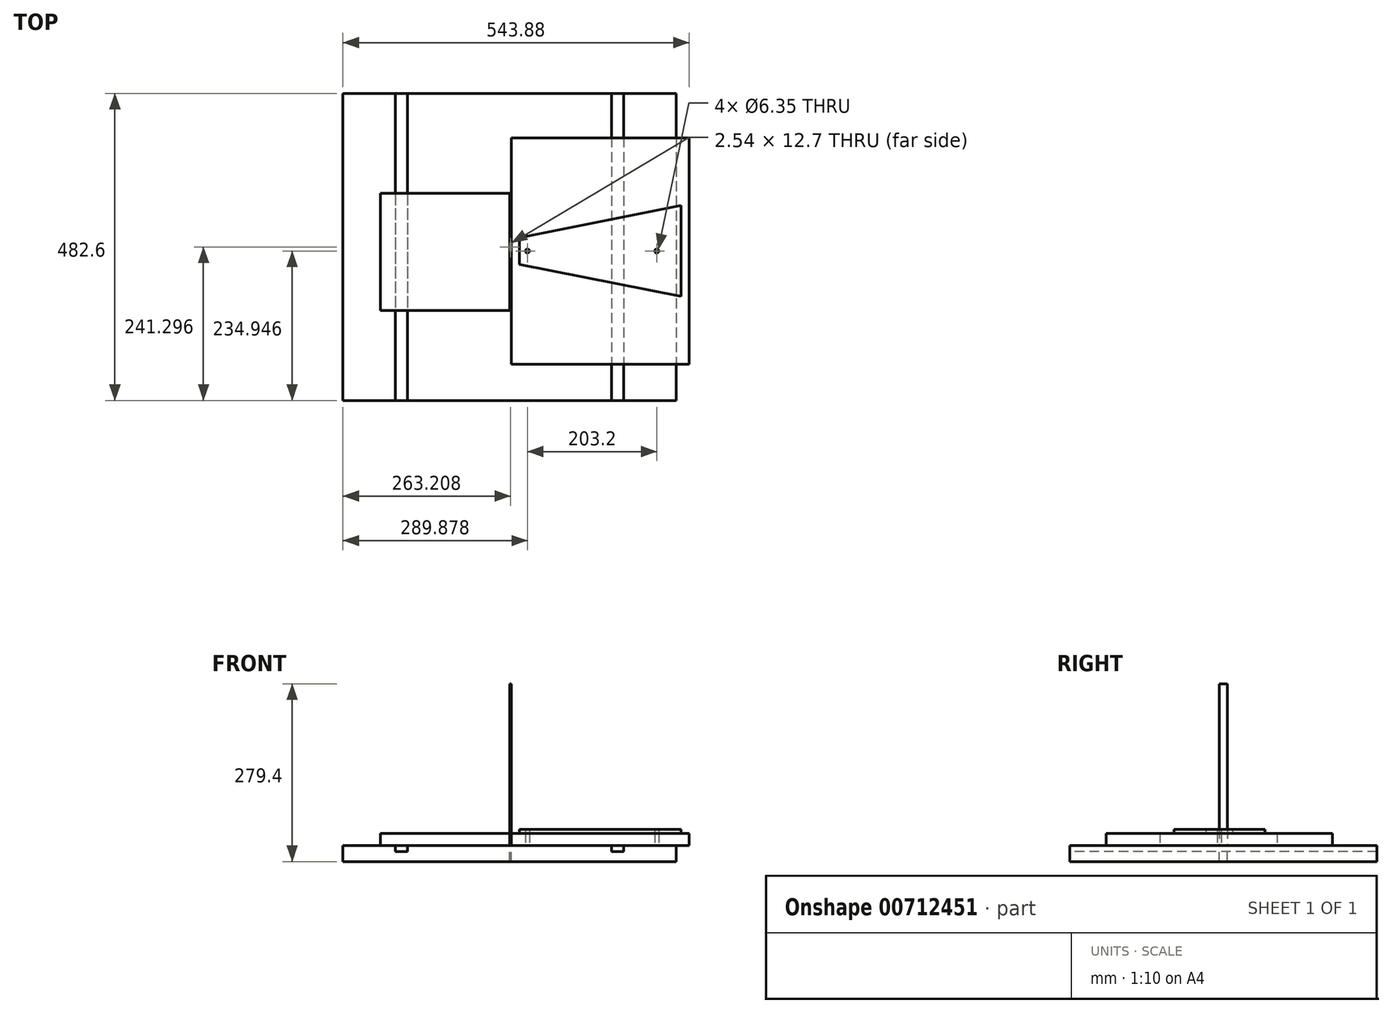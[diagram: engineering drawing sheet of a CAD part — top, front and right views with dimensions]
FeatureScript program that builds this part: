
annotation { "Feature Type Name" : "Feature", "Feature Type Description" : "" }
export const myFeature = defineFeature(function(context is Context, id is Id, definition is map)
    precondition{}
    {
        {
            var Q0;
            Q0=qCreatedBy(makeId("Top.planeOp"),FACE);
            var sketch = newSketch(context, id + "F0", { "sketchPlane" : qUnion([Q0])});
            skLineSegment(sketch, "E0.bottom", {"start": v(-188.77, 300.77) * mm, "end": v(131.9, 300.77) * mm});
            skLineSegment(sketch, "E0.top", {"start": v(-188.77, -181.83) * mm, "end": v(131.9, -181.83) * mm});
            skLineSegment(sketch, "E0.left", {"start": v(-188.77, 300.77) * mm, "end": v(-188.77, -181.83) * mm});
            skLineSegment(sketch, "E0.right", {"start": v(131.9, 300.77) * mm, "end": v(131.9, -181.83) * mm});
            skLineSegment(sketch, "E1.bottom", {"start": v(131.9, 300.77) * mm, "end": v(150.96, 300.77) * mm});
            skLineSegment(sketch, "E1.top", {"start": v(131.9, -181.83) * mm, "end": v(150.96, -181.83) * mm});
            skLineSegment(sketch, "E1.right", {"start": v(150.96, 300.77) * mm, "end": v(150.96, -181.83) * mm});
            skLineSegment(sketch, "E2.bottom", {"start": v(-188.77, 300.77) * mm, "end": v(-207.82, 300.77) * mm});
            skLineSegment(sketch, "E2.top", {"start": v(-188.77, -181.83) * mm, "end": v(-207.82, -181.83) * mm});
            skLineSegment(sketch, "E2.right", {"start": v(-207.82, 300.77) * mm, "end": v(-207.82, -181.83) * mm});
            skLineSegment(sketch, "E3.bottom", {"start": v(150.96, 300.77) * mm, "end": v(233.5, 300.77) * mm});
            skLineSegment(sketch, "E3.top", {"start": v(150.96, -181.83) * mm, "end": v(233.5, -181.83) * mm});
            skLineSegment(sketch, "E3.right", {"start": v(233.5, 300.77) * mm, "end": v(233.5, -181.83) * mm});
            skLineSegment(sketch, "E4.bottom", {"start": v(-207.82, 300.77) * mm, "end": v(-290.37, 300.77) * mm});
            skLineSegment(sketch, "E4.top", {"start": v(-207.82, -181.83) * mm, "end": v(-290.37, -181.83) * mm});
            skLineSegment(sketch, "E4.right", {"start": v(-290.37, 300.77) * mm, "end": v(-290.37, -181.83) * mm});
            skLineSegment(sketch, "E5.bottom", {"start": v(-28.43, 53.12) * mm, "end": v(-25.9, 53.12) * mm});
            skLineSegment(sketch, "E5.top", {"start": v(-28.43, 65.82) * mm, "end": v(-25.9, 65.82) * mm});
            skLineSegment(sketch, "E5.left", {"start": v(-28.43, 53.12) * mm, "end": v(-28.43, 65.82) * mm});
            skLineSegment(sketch, "E5.right", {"start": v(-25.9, 53.12) * mm, "end": v(-25.9, 65.82) * mm});
            skSolve(sketch);
        }
        {
            var Q0;
            Q0=makeQuery(id+"F0.imprint","IMPRINT",FACE,{"disambiguationData":[TD([[makeQuery(id+"F0.imprint","IMPRINT",EDGE,{"derivedFrom":sQuery(id+"F0.wireOp",EDGE,"E3.bottom")}),-1.0]])]});
            var Q1;
            Q1=makeQuery(id+"F0.imprint","IMPRINT",FACE,{"disambiguationData":[TD([[makeQuery(id+"F0.imprint","IMPRINT",EDGE,{"derivedFrom":sQuery(id+"F0.wireOp",EDGE,"E0.bottom")}),-1.0]])]});
            var Q2;
            Q2=makeQuery(id+"F0.imprint","IMPRINT",FACE,{"disambiguationData":[TD([[makeQuery(id+"F0.imprint","IMPRINT",EDGE,{"derivedFrom":sQuery(id+"F0.wireOp",EDGE,"E4.bottom")}),1.0]])]});
            var Q3;
            Q3=makeQuery(id+"F0.imprint","IMPRINT",FACE,{"disambiguationData":[TD([[makeQuery(id+"F0.imprint","IMPRINT",EDGE,{"derivedFrom":sQuery(id+"F0.wireOp",EDGE,"E2.bottom")}),1.0]])]});
            var Q4;
            Q4=makeQuery(id+"F0.imprint","IMPRINT",FACE,{"disambiguationData":[TD([[makeQuery(id+"F0.imprint","IMPRINT",EDGE,{"derivedFrom":sQuery(id+"F0.wireOp",EDGE,"E1.bottom")}),-1.0]])]});
            extrude(context, id + "F1", {"entities" : qUnion([Q0, Q1, Q2, Q3, Q4]), "oppositeDirection" : true, "depth" : 25.4 * mm, "offsetDistance" : 25.4 * mm});
        }
        {
            var Q0;
            Q0=makeQuery(id+"F0.imprint","IMPRINT",FACE,{"disambiguationData":[TD([[makeQuery(id+"F0.imprint","IMPRINT",EDGE,{"derivedFrom":sQuery(id+"F0.wireOp",EDGE,"E2.bottom")}),1.0]])]});
            var Q1;
            Q1=makeQuery(id+"F0.imprint","IMPRINT",FACE,{"disambiguationData":[TD([[makeQuery(id+"F0.imprint","IMPRINT",EDGE,{"derivedFrom":sQuery(id+"F0.wireOp",EDGE,"E1.bottom")}),-1.0]])]});
            extrude(context, id + "F2", {"entities" : qUnion([Q0, Q1]), "operationType" : NewBodyOperationType.REMOVE, "oppositeDirection" : true, "depth" : 9.52 * mm, "offsetDistance" : 25.4 * mm});
        }
        {
            var Q0;
            Q0=makeQuery(id+"F0.imprint","IMPRINT",FACE,{"disambiguationData":[TD([[makeQuery(id+"F0.imprint","IMPRINT",EDGE,{"derivedFrom":sQuery(id+"F0.wireOp",EDGE,"E5.bottom")}),1.0]])]});
            extrude(context, id + "F3", {"entities" : qUnion([Q0]), "depth" : 254 * mm, "offsetDistance" : 25.4 * mm});
        }
        {
            var Q0;
            {var subQ0=sQuery(id+"F0.wireOp",EDGE,"E5.bottom");var subQ1=sQuery(id+"F0.wireOp",EDGE,"E4.top");var subQ2=sQuery(id+"F0.wireOp",EDGE,"E3.top");var subQ3=sQuery(id+"F0.wireOp",EDGE,"E2.top");var subQ4=sQuery(id+"F0.wireOp",EDGE,"E1.top");var subQ5=sQuery(id+"F0.wireOp",EDGE,"E0.top");var subQ6=sQuery(id+"F0.wireOp",EDGE,"E5.top");var subQ7=sQuery(id+"F0.wireOp",EDGE,"E4.bottom");var subQ8=sQuery(id+"F0.wireOp",EDGE,"E3.bottom");var subQ9=sQuery(id+"F0.wireOp",EDGE,"E2.bottom");var subQ10=sQuery(id+"F0.wireOp",EDGE,"E1.bottom");var subQ11=sQuery(id+"F0.wireOp",EDGE,"E0.bottom");var subQ12=sQuery(id+"F0.wireOp",EDGE,"E5.left");var subQ13=sQuery(id+"F0.wireOp",EDGE,"E5.right");Q0=makeQuery(id+"F2.boolean.opBoolean","SPLIT",FACE,{"disambiguationData":[TD([makeQuery(id+"F1.opExtrude","SWEPT_FACE",FACE,{"disambiguationData":[OSD([subQ0])]})])],"derivedFrom":makeQuery(id+"F1.opExtrude","CAP_FACE",FACE,{"disambiguationData":[OSD([subQ11,subQ5,subQ10,subQ4,subQ9,subQ3,subQ8,subQ2,sQuery(id+"F0.wireOp",EDGE,"E3.right"),subQ7,subQ1,sQuery(id+"F0.wireOp",EDGE,"E4.right"),subQ0,subQ6,subQ12,subQ13])],"isStart":true})});}
            var sketch = newSketch(context, id + "F4", { "sketchPlane" : qUnion([Q0])});
            skLineSegment(sketch, "E6.bottom", {"start": v(-25.9, 230.92) * mm, "end": v(253.5, 230.92) * mm});
            skLineSegment(sketch, "E6.top", {"start": v(-25.9, -124.68) * mm, "end": v(253.5, -124.68) * mm});
            skLineSegment(sketch, "E6.left", {"start": v(-25.9, 230.92) * mm, "end": v(-25.9, -124.68) * mm});
            skLineSegment(sketch, "E6.right", {"start": v(253.5, 230.92) * mm, "end": v(253.5, -124.68) * mm});
            skLineSegment(sketch, "E7", {"start": v(-311.08, 53.12) * mm, "end": v(256.92, 53.12) * mm, "construction": true});
            skLineSegment(sketch, "E8.bottom", {"start": v(-231.63, 143.61) * mm, "end": v(-28.43, 143.61) * mm});
            skLineSegment(sketch, "E8.top", {"start": v(-231.63, -40.52) * mm, "end": v(-28.43, -40.52) * mm});
            skLineSegment(sketch, "E8.left", {"start": v(-231.63, 143.61) * mm, "end": v(-231.63, -40.52) * mm});
            skLineSegment(sketch, "E8.right", {"start": v(-28.43, 143.61) * mm, "end": v(-28.43, -40.52) * mm});
            skCircle(sketch, "E9", {"center": v(-0.5, 53.12) * mm, "radius": 3.18 * mm});
            skCircle(sketch, "E10", {"center": v(202.7, 53.12) * mm, "radius": 3.17 * mm});
            skSolve(sketch);
        }
        {
            var Q0;
            Q0=makeQuery(id+"F4.imprint","IMPRINT",FACE,{"disambiguationData":[TD([[makeQuery(id+"F4.imprint","IMPRINT",EDGE,{"derivedFrom":sQuery(id+"F4.wireOp",EDGE,"E9")}),-1.0]])]});
            var Q1;
            {var subQ0=sQuery(id+"F4.wireOp",EDGE,"E6.right");Q1=makeQuery(id+"F4.imprint","IMPRINT",FACE,{"disambiguationData":[TD([[makeQuery(id+"F4.imprint","IMPRINT",EDGE,{"derivedFrom":subQ0}),-1.0]])]});}
            extrude(context, id + "F5", {"entities" : qUnion([Q0, Q1]), "depth" : 19.05 * mm, "offsetDistance" : 25.4 * mm});
        }
        {
            var Q0;
            {var subQ0=sQuery(id+"F4.wireOp",EDGE,"E8.right");var subQ2=sQuery(id+"F4.wireOp",EDGE,"E8.bottom");var subQ3=makeQuery(id+"F4.imprint","INTERSECT",VERTEX,{"derivedFrom":[subQ2,subQ0]});Q0=makeQuery(id+"F4.imprint","IMPRINT",FACE,{"disambiguationData":[TD([[makeQuery(id+"F4.imprint","IMPRINT",EDGE,{"disambiguationData":[TD([[subQ3,1.0]])],"derivedFrom":subQ2}),-1.0]])]});}
            var Q1;
            {var subQ0=sQuery(id+"F4.wireOp",EDGE,"E8.left");Q1=makeQuery(id+"F4.imprint","IMPRINT",FACE,{"disambiguationData":[TD([[makeQuery(id+"F4.imprint","IMPRINT",EDGE,{"derivedFrom":subQ0}),1.0]])]});}
            extrude(context, id + "F6", {"entities" : qUnion([Q0, Q1]), "depth" : 19.05 * mm, "offsetDistance" : 25.4 * mm});
        }
        {
            var Q0;
            Q0=makeQuery(id+"F5.opExtrude","CAP_FACE",FACE,{"disambiguationData":[OSD([sQuery(id+"F4.wireOp",EDGE,"E6.bottom"),sQuery(id+"F4.wireOp",EDGE,"E6.top"),sQuery(id+"F4.wireOp",EDGE,"E6.left"),sQuery(id+"F4.wireOp",EDGE,"E6.right"),sQuery(id+"F4.wireOp",EDGE,"E9")])],"isStart":false});
            var sketch = newSketch(context, id + "F7", { "sketchPlane" : qUnion([Q0])});
            skLineSegment(sketch, "E11", {"start": v(-13.2, 74.07) * mm, "end": v(-13.2, 32.16) * mm});
            skLineSegment(sketch, "E12", {"start": v(-13.2, 32.16) * mm, "end": v(240.8, -18.36) * mm});
            skLineSegment(sketch, "E13", {"start": v(240.8, -18.36) * mm, "end": v(240.8, 124.6) * mm});
            skLineSegment(sketch, "E14", {"start": v(240.8, 124.6) * mm, "end": v(-13.2, 74.07) * mm});
            skCircle(sketch, "E15", {"center": v(-0.5, 53.12) * mm, "radius": 3.18 * mm});
            skLineSegment(sketch, "E16", {"start": v(-0.5, 53.12) * mm, "end": v(165.88, 53.12) * mm, "construction": true});
            skCircle(sketch, "E17", {"center": v(202.7, 53.12) * mm, "radius": 3.18 * mm});
            skSolve(sketch);
        }
        {
            var Q0;
            Q0 = qSketchRegion(id + "F7", true);
            extrude(context, id + "F8", {"entities" : qUnion([Q0]), "depth" : 6.35 * mm, "offsetDistance" : 25.4 * mm});
        }
    });
